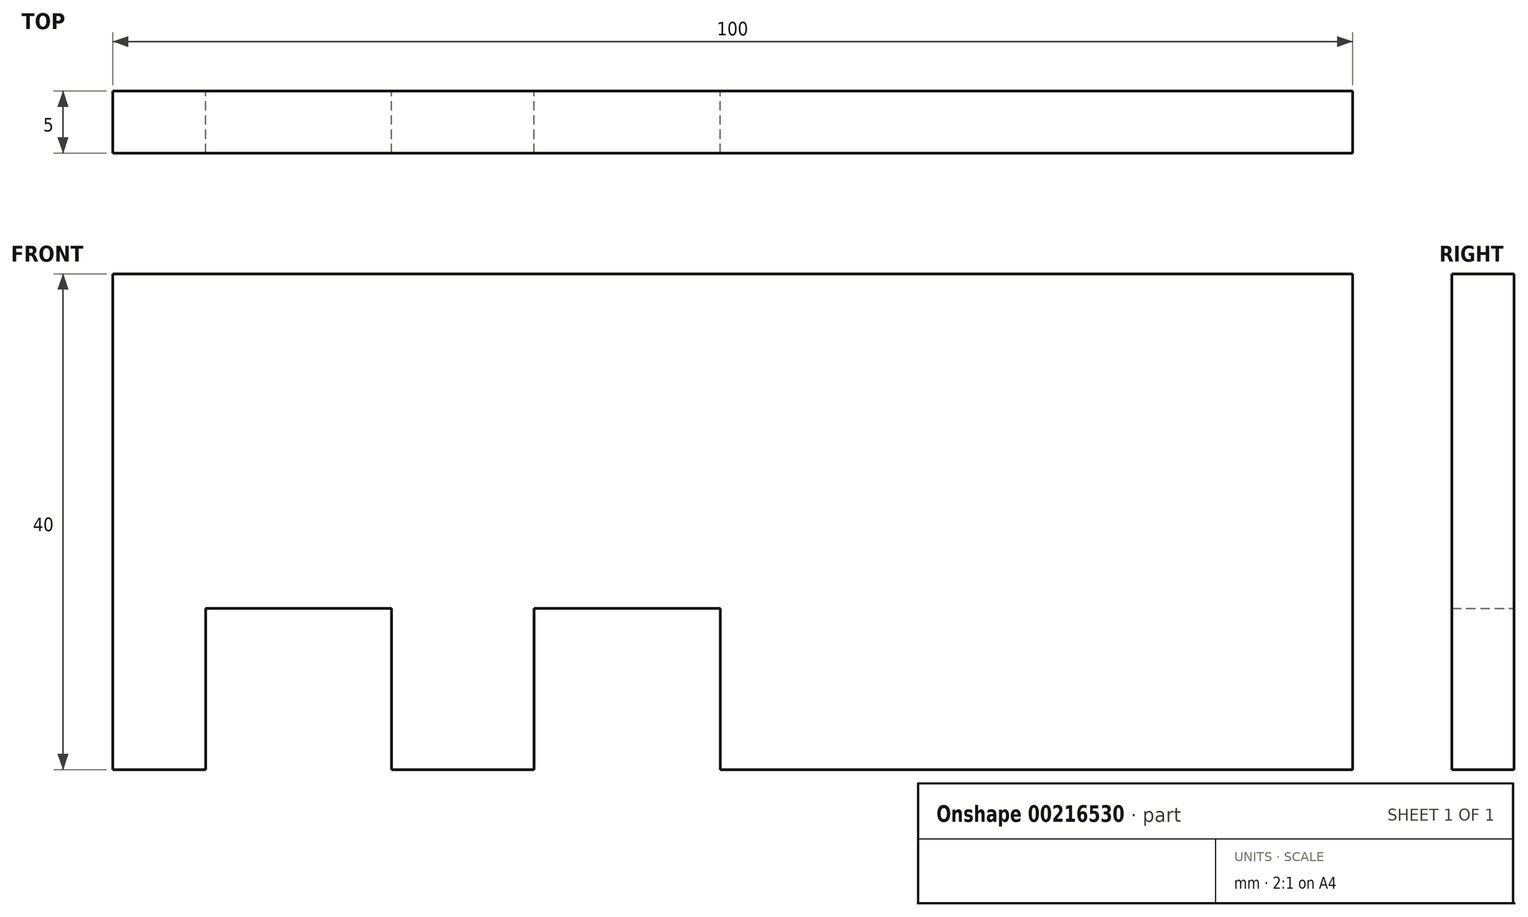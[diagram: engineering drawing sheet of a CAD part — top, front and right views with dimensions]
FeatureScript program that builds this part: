
annotation { "Feature Type Name" : "Feature", "Feature Type Description" : "" }
export const myFeature = defineFeature(function(context is Context, id is Id, definition is map)
    precondition{}
    {
        {
            var Q0;
            Q0=qCreatedBy(makeId("Front.planeOp"),FACE);
            var sketch = newSketch(context, id + "F0", { "sketchPlane" : qUnion([Q0])});
            skLineSegment(sketch, "E0.bottom", {"start": v(-49.86, 25.34) * mm, "end": v(50.14, 25.34) * mm});
            skLineSegment(sketch, "E0.top", {"start": v(-49.86, -14.66) * mm, "end": v(50.14, -14.66) * mm});
            skLineSegment(sketch, "E0.left", {"start": v(-49.86, 25.34) * mm, "end": v(-49.86, -14.66) * mm});
            skLineSegment(sketch, "E0.right", {"start": v(50.14, 25.34) * mm, "end": v(50.14, -14.66) * mm});
            skLineSegment(sketch, "E1.bottom", {"start": v(-15.86, -14.66) * mm, "end": v(-0.86, -14.66) * mm});
            skLineSegment(sketch, "E1.top", {"start": v(-15.86, -1.66) * mm, "end": v(-0.86, -1.66) * mm});
            skLineSegment(sketch, "E1.left", {"start": v(-15.86, -14.66) * mm, "end": v(-15.86, -1.66) * mm});
            skLineSegment(sketch, "E1.right", {"start": v(-0.86, -14.66) * mm, "end": v(-0.86, -1.66) * mm});
            skLineSegment(sketch, "E2.bottom", {"start": v(-42.36, -14.66) * mm, "end": v(-27.36, -14.66) * mm});
            skLineSegment(sketch, "E2.top", {"start": v(-42.36, -1.66) * mm, "end": v(-27.36, -1.66) * mm});
            skLineSegment(sketch, "E2.left", {"start": v(-42.36, -14.66) * mm, "end": v(-42.36, -1.66) * mm});
            skLineSegment(sketch, "E2.right", {"start": v(-27.36, -14.66) * mm, "end": v(-27.36, -1.66) * mm});
            skSolve(sketch);
        }
        {
            var Q0;
            Q0=makeQuery(id+"F0.imprint","IMPRINT",FACE,{"disambiguationData":[TD([[makeQuery(id+"F0.imprint","IMPRINT",EDGE,{"derivedFrom":sQuery(id+"F0.wireOp",EDGE,"E0.bottom")}),-1.0]])]});
            extrude(context, id + "F1", {"entities" : qUnion([Q0]), "depth" : 5 * mm});
        }
    });
